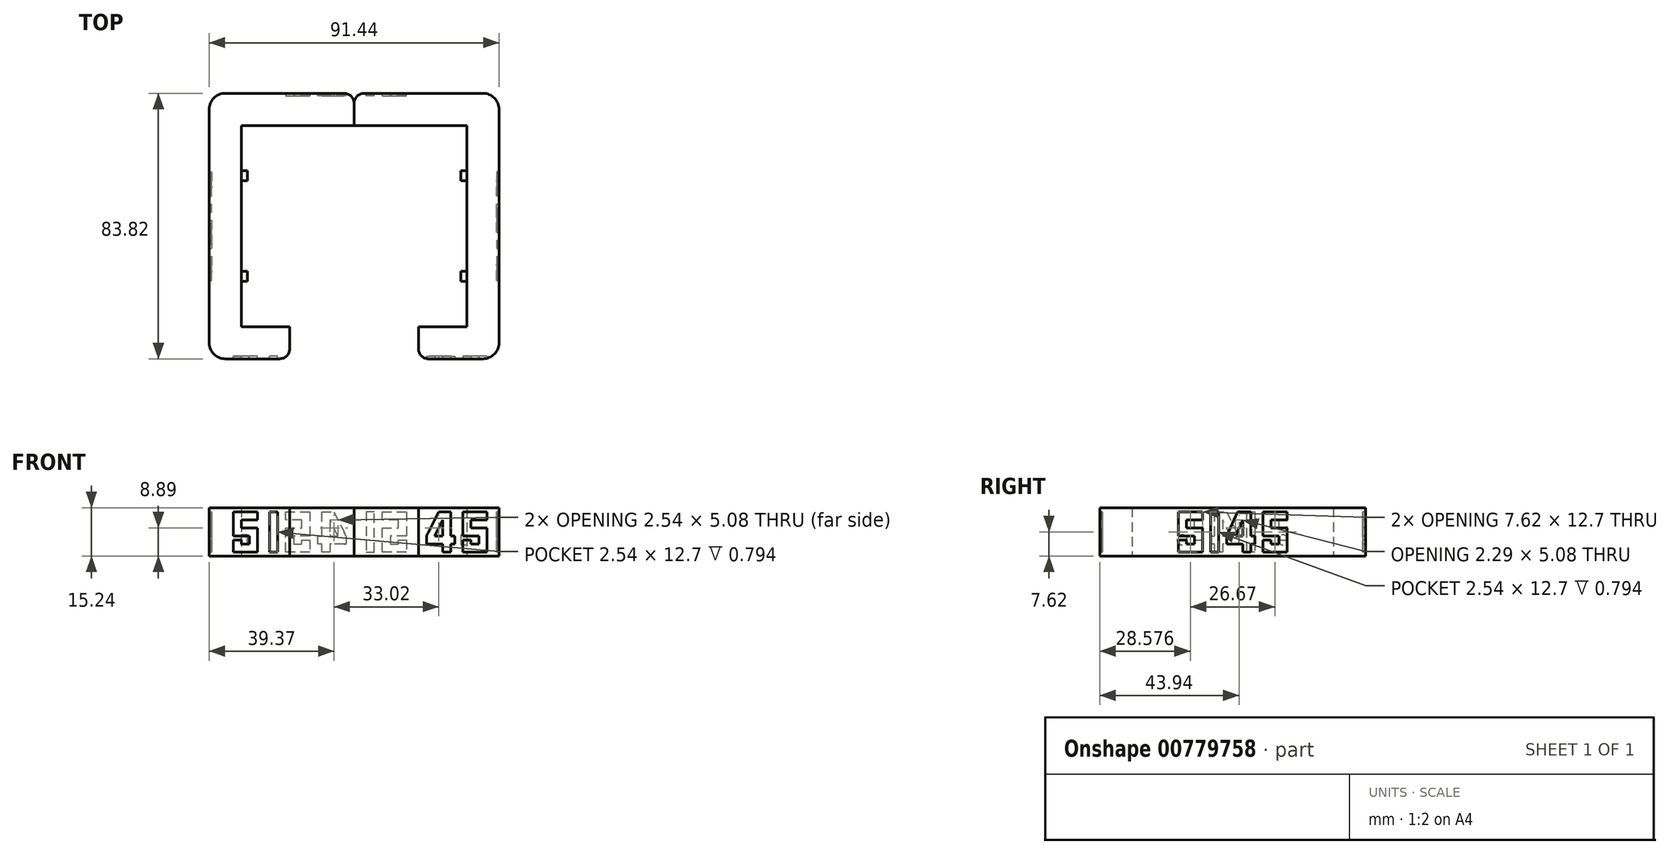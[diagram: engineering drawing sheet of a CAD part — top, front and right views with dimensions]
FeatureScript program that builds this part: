
annotation { "Feature Type Name" : "Feature", "Feature Type Description" : "" }
export const myFeature = defineFeature(function(context is Context, id is Id, definition is map)
    precondition{}
    {
        {
            var Q0;
            Q0=qCreatedBy(makeId("Top.planeOp"),FACE);
            var sketch = newSketch(context, id + "F0", { "sketchPlane" : qUnion([Q0])});
            skLineSegment(sketch, "E0", {"start": v(0, 28.67) * mm, "end": v(0, 38.83) * mm});
            skLineSegment(sketch, "E1", {"start": v(0, 38.83) * mm, "end": v(45.72, 38.83) * mm});
            skLineSegment(sketch, "E2", {"start": v(45.72, 38.83) * mm, "end": v(45.72, -44.99) * mm});
            skLineSegment(sketch, "E3", {"start": v(45.72, -44.99) * mm, "end": v(20.32, -44.99) * mm});
            skLineSegment(sketch, "E4", {"start": v(20.32, -44.99) * mm, "end": v(20.32, -34.83) * mm});
            skLineSegment(sketch, "E5", {"start": v(20.32, -34.83) * mm, "end": v(35.56, -34.83) * mm});
            skLineSegment(sketch, "E6", {"start": v(35.56, -34.83) * mm, "end": v(35.56, 28.67) * mm});
            skLineSegment(sketch, "E7", {"start": v(35.56, 28.67) * mm, "end": v(0, 28.67) * mm});
            skSolve(sketch);
        }
        {
            var Q0;
            Q0=makeQuery(id+"F0.imprint","IMPRINT",FACE,{"disambiguationData":[TD([[makeQuery(id+"F0.imprint","IMPRINT",EDGE,{"derivedFrom":sQuery(id+"F0.wireOp",EDGE,"E0")}),-1.0]])]});
            extrude(context, id + "F1", {"entities" : qUnion([Q0]), "depth" : 15.24 * mm, "offsetDistance" : 25.4 * mm});
        }
        {
            var Q0;
            Q0=makeQuery(id+"F1.opExtrude","SWEPT_FACE",FACE,{"disambiguationData":[OSD([sQuery(id+"F0.wireOp",EDGE,"E6")])]});
            var sketch = newSketch(context, id + "F2", { "sketchPlane" : qUnion([Q0])});
            skCircle(sketch, "E8", {"center": v(-12.8, 5.08) * mm, "radius": 1.59 * mm});
            skPoint(sketch, "E8.centerSnap0", {"position": v(-28.67, 5.08) * mm});
            skCircle(sketch, "E9", {"center": v(18.95, 5.08) * mm, "radius": 1.59 * mm});
            skPoint(sketch, "E9.centerSnap0", {"position": v(34.83, 5.08) * mm});
            skSolve(sketch);
        }
        {
            var Q0;
            Q0=makeQuery(id+"F2.imprint","IMPRINT",FACE,{"disambiguationData":[TD([[makeQuery(id+"F2.imprint","IMPRINT",EDGE,{"derivedFrom":sQuery(id+"F2.wireOp",EDGE,"E8")}),1.0]])]});
            var Q1;
            Q1=makeQuery(id+"F2.imprint","IMPRINT",FACE,{"disambiguationData":[TD([[makeQuery(id+"F2.imprint","IMPRINT",EDGE,{"derivedFrom":sQuery(id+"F2.wireOp",EDGE,"E9")}),1.0]])]});
            extrude(context, id + "F3", {"entities" : qUnion([Q0, Q1]), "operationType" : NewBodyOperationType.ADD, "depth" : 1.9 * mm, "offsetDistance" : 25.4 * mm});
        }
        {
            var Q0;
            Q0=qCreatedBy(makeId("Top.planeOp"),FACE);
            var sketch = newSketch(context, id + "F4", { "sketchPlane" : qUnion([Q0])});
            skLineSegment(sketch, "E10", {"start": v(0, 28.67) * mm, "end": v(-35.56, 28.67) * mm});
            skLineSegment(sketch, "E11", {"start": v(-35.56, 28.67) * mm, "end": v(-35.56, -34.83) * mm});
            skLineSegment(sketch, "E12", {"start": v(-35.56, -34.83) * mm, "end": v(-20.32, -34.83) * mm});
            skLineSegment(sketch, "E13", {"start": v(-20.32, -34.83) * mm, "end": v(-20.32, -44.99) * mm});
            skLineSegment(sketch, "E14", {"start": v(-20.32, -44.99) * mm, "end": v(-45.72, -44.99) * mm});
            skLineSegment(sketch, "E15", {"start": v(-45.72, -44.99) * mm, "end": v(-45.72, 38.83) * mm});
            skLineSegment(sketch, "E16", {"start": v(-45.72, 38.83) * mm, "end": v(0, 38.83) * mm});
            skLineSegment(sketch, "E17", {"start": v(0, 38.83) * mm, "end": v(0, 28.67) * mm});
            skSolve(sketch);
        }
        {
            var Q0;
            Q0=makeQuery(id+"F4.imprint","IMPRINT",FACE,{"disambiguationData":[TD([[makeQuery(id+"F4.imprint","IMPRINT",EDGE,{"derivedFrom":sQuery(id+"F4.wireOp",EDGE,"E10")}),-1.0]])]});
            extrude(context, id + "F5", {"entities" : qUnion([Q0]), "depth" : 15.24 * mm, "offsetDistance" : 25.4 * mm});
        }
        {
            var Q0;
            Q0=makeQuery(id+"F5.opExtrude","SWEPT_FACE",FACE,{"disambiguationData":[OSD([sQuery(id+"F4.wireOp",EDGE,"E11")])]});
            var sketch = newSketch(context, id + "F6", { "sketchPlane" : qUnion([Q0])});
            skCircle(sketch, "E18", {"center": v(-18.95, 5.08) * mm, "radius": 1.59 * mm});
            skPoint(sketch, "E18.centerSnap0", {"position": v(-34.83, 7.62) * mm});
            skCircle(sketch, "E19", {"center": v(12.8, 5.08) * mm, "radius": 1.59 * mm});
            skSolve(sketch);
        }
        {
            var Q0;
            Q0=makeQuery(id+"F6.imprint","IMPRINT",FACE,{"disambiguationData":[TD([[makeQuery(id+"F6.imprint","IMPRINT",EDGE,{"derivedFrom":sQuery(id+"F6.wireOp",EDGE,"E19")}),1.0]])]});
            var Q1;
            Q1=makeQuery(id+"F6.imprint","IMPRINT",FACE,{"disambiguationData":[TD([[makeQuery(id+"F6.imprint","IMPRINT",EDGE,{"derivedFrom":sQuery(id+"F6.wireOp",EDGE,"E18")}),1.0]])]});
            extrude(context, id + "F7", {"entities" : qUnion([Q0, Q1]), "operationType" : NewBodyOperationType.ADD, "depth" : 1.9 * mm, "offsetDistance" : 25.4 * mm});
        }
        {
            var Q0;
            Q0=makeQuery(id+"F1.opExtrude","SWEPT_FACE",FACE,{"disambiguationData":[OSD([sQuery(id+"F0.wireOp",EDGE,"E2")])]});
            var sketch = newSketch(context, id + "F8", { "sketchPlane" : qUnion([Q0])});
            skLineSegment(sketch, "E20", {"start": v(-12.6, 13.97) * mm, "end": v(-20.22, 13.97) * mm});
            skLineSegment(sketch, "E21", {"start": v(-20.22, 13.97) * mm, "end": v(-20.22, 6.35) * mm});
            skLineSegment(sketch, "E22", {"start": v(-20.22, 6.35) * mm, "end": v(-15.14, 6.35) * mm});
            skLineSegment(sketch, "E23", {"start": v(-15.14, 6.35) * mm, "end": v(-15.14, 3.81) * mm});
            skLineSegment(sketch, "E24", {"start": v(-15.14, 3.8) * mm, "end": v(-17.68, 3.8) * mm});
            skLineSegment(sketch, "E25", {"start": v(-17.68, 3.81) * mm, "end": v(-17.68, 5.08) * mm});
            skLineSegment(sketch, "E26", {"start": v(-17.68, 5.08) * mm, "end": v(-20.22, 5.08) * mm});
            skLineSegment(sketch, "E27", {"start": v(-20.22, 5.08) * mm, "end": v(-20.22, 1.27) * mm});
            skLineSegment(sketch, "E28", {"start": v(-20.22, 1.27) * mm, "end": v(-12.6, 1.27) * mm});
            skLineSegment(sketch, "E29", {"start": v(-12.6, 1.27) * mm, "end": v(-12.6, 8.9) * mm});
            skLineSegment(sketch, "E30", {"start": v(-12.6, 8.89) * mm, "end": v(-17.68, 8.89) * mm});
            skLineSegment(sketch, "E31", {"start": v(-17.68, 8.9) * mm, "end": v(-17.68, 11.43) * mm});
            skLineSegment(sketch, "E32", {"start": v(-17.68, 11.43) * mm, "end": v(-12.6, 11.43) * mm});
            skLineSegment(sketch, "E33", {"start": v(-12.6, 11.43) * mm, "end": v(-12.6, 13.97) * mm});
            skLineSegment(sketch, "E34", {"start": v(-10.06, 13.97) * mm, "end": v(-10.06, 1.27) * mm});
            skLineSegment(sketch, "E35", {"start": v(-10.06, 1.27) * mm, "end": v(-7.52, 1.27) * mm});
            skLineSegment(sketch, "E36", {"start": v(-7.52, 1.27) * mm, "end": v(-7.52, 13.97) * mm});
            skLineSegment(sketch, "E37", {"start": v(-7.52, 13.97) * mm, "end": v(-10.06, 13.97) * mm});
            skLineSegment(sketch, "E38", {"start": v(-1.54, 13.97) * mm, "end": v(-4.98, 6.35) * mm});
            skLineSegment(sketch, "E39", {"start": v(-4.98, 6.35) * mm, "end": v(-4.98, 3.81) * mm});
            skLineSegment(sketch, "E40", {"start": v(-4.98, 3.81) * mm, "end": v(0.1, 3.81) * mm});
            skLineSegment(sketch, "E41", {"start": v(0.1, 3.81) * mm, "end": v(0.1, 1.27) * mm});
            skLineSegment(sketch, "E42", {"start": v(0.1, 1.27) * mm, "end": v(2.64, 1.27) * mm});
            skLineSegment(sketch, "E43", {"start": v(2.64, 1.27) * mm, "end": v(2.64, 3.81) * mm});
            skLineSegment(sketch, "E44", {"start": v(2.64, 3.81) * mm, "end": v(3.9, 3.81) * mm});
            skLineSegment(sketch, "E45", {"start": v(3.9, 3.81) * mm, "end": v(3.9, 6.35) * mm});
            skLineSegment(sketch, "E46", {"start": v(3.9, 6.35) * mm, "end": v(2.64, 6.35) * mm});
            skLineSegment(sketch, "E47", {"start": v(2.64, 6.35) * mm, "end": v(2.64, 13.97) * mm});
            skLineSegment(sketch, "E48", {"start": v(2.64, 13.97) * mm, "end": v(-1.54, 13.97) * mm});
            skLineSegment(sketch, "E49", {"start": v(0.1, 6.35) * mm, "end": v(-2.2, 6.35) * mm});
            skLineSegment(sketch, "E50", {"start": v(-2.2, 6.35) * mm, "end": v(0.1, 11.43) * mm});
            skLineSegment(sketch, "E51", {"start": v(0.1, 11.43) * mm, "end": v(0.1, 6.35) * mm});
            skLineSegment(sketch, "E52", {"start": v(14.07, 13.97) * mm, "end": v(6.45, 13.97) * mm});
            skLineSegment(sketch, "E53", {"start": v(6.45, 13.97) * mm, "end": v(6.45, 6.35) * mm});
            skLineSegment(sketch, "E54", {"start": v(6.45, 6.35) * mm, "end": v(11.53, 6.35) * mm});
            skLineSegment(sketch, "E55", {"start": v(11.53, 6.35) * mm, "end": v(11.53, 3.81) * mm});
            skLineSegment(sketch, "E56", {"start": v(11.53, 3.81) * mm, "end": v(8.99, 3.81) * mm});
            skPoint(sketch, "E56.endSnap0", {"position": v(8.99, 6.35) * mm});
            skLineSegment(sketch, "E57", {"start": v(8.99, 3.81) * mm, "end": v(8.99, 5.08) * mm});
            skPoint(sketch, "E57.endSnap0", {"position": v(11.53, 5.08) * mm});
            skLineSegment(sketch, "E58", {"start": v(8.99, 5.08) * mm, "end": v(6.45, 5.08) * mm});
            skLineSegment(sketch, "E59", {"start": v(6.45, 5.08) * mm, "end": v(6.45, 1.27) * mm});
            skLineSegment(sketch, "E60", {"start": v(6.45, 1.27) * mm, "end": v(14.07, 1.27) * mm});
            skLineSegment(sketch, "E61", {"start": v(14.07, 1.27) * mm, "end": v(14.07, 8.9) * mm});
            skLineSegment(sketch, "E62", {"start": v(14.07, 8.9) * mm, "end": v(8.99, 8.9) * mm});
            skLineSegment(sketch, "E63", {"start": v(8.99, 8.9) * mm, "end": v(8.99, 11.43) * mm});
            skLineSegment(sketch, "E64", {"start": v(8.99, 11.43) * mm, "end": v(14.07, 11.43) * mm});
            skLineSegment(sketch, "E65", {"start": v(14.07, 11.43) * mm, "end": v(14.07, 13.97) * mm});
            skLineSegment(sketch, "E66", {"start": v(-20.22, 13.97) * mm, "end": v(-44.99, 13.97) * mm});
            skLineSegment(sketch, "E67", {"start": v(14.07, 13.97) * mm, "end": v(38.83, 13.97) * mm});
            skSolve(sketch);
        }
        {
            var Q0;
            Q0=makeQuery(id+"F8.imprint","IMPRINT",FACE,{"disambiguationData":[TD([[makeQuery(id+"F8.imprint","IMPRINT",EDGE,{"derivedFrom":sQuery(id+"F8.wireOp",EDGE,"E20")}),1.0]])]});
            var Q1;
            Q1=makeQuery(id+"F8.imprint","IMPRINT",FACE,{"disambiguationData":[TD([[makeQuery(id+"F8.imprint","IMPRINT",EDGE,{"derivedFrom":sQuery(id+"F8.wireOp",EDGE,"E34")}),1.0]])]});
            var Q2;
            Q2=makeQuery(id+"F8.imprint","IMPRINT",FACE,{"disambiguationData":[TD([[makeQuery(id+"F8.imprint","IMPRINT",EDGE,{"derivedFrom":sQuery(id+"F8.wireOp",EDGE,"E38")}),1.0]])]});
            var Q3;
            Q3=makeQuery(id+"F8.imprint","IMPRINT",FACE,{"disambiguationData":[TD([[makeQuery(id+"F8.imprint","IMPRINT",EDGE,{"derivedFrom":sQuery(id+"F8.wireOp",EDGE,"E52")}),1.0]])]});
            extrude(context, id + "F9", {"entities" : qUnion([Q0, Q1, Q2, Q3]), "operationType" : NewBodyOperationType.REMOVE, "oppositeDirection" : true, "depth" : 0.8 * mm, "offsetDistance" : 25.4 * mm});
        }
        {
            var Q0;
            Q0=makeQuery(id+"F1.opExtrude","SWEPT_FACE",FACE,{"disambiguationData":[OSD([sQuery(id+"F0.wireOp",EDGE,"E3")])]});
            var sketch = newSketch(context, id + "F10", { "sketchPlane" : qUnion([Q0])});
            skLineSegment(sketch, "E68", {"start": v(22.86, 6.35) * mm, "end": v(22.86, 3.81) * mm});
            skLineSegment(sketch, "E69", {"start": v(22.86, 3.81) * mm, "end": v(27.94, 3.81) * mm});
            skLineSegment(sketch, "E70", {"start": v(27.94, 3.81) * mm, "end": v(27.94, 1.27) * mm});
            skLineSegment(sketch, "E71", {"start": v(27.94, 1.27) * mm, "end": v(30.48, 1.27) * mm});
            skLineSegment(sketch, "E72", {"start": v(30.48, 1.27) * mm, "end": v(30.48, 3.81) * mm});
            skLineSegment(sketch, "E73", {"start": v(30.48, 3.81) * mm, "end": v(31.75, 3.81) * mm});
            skLineSegment(sketch, "E74", {"start": v(31.75, 3.81) * mm, "end": v(31.75, 6.35) * mm});
            skLineSegment(sketch, "E75", {"start": v(31.75, 6.35) * mm, "end": v(30.48, 6.35) * mm});
            skLineSegment(sketch, "E76", {"start": v(30.48, 6.35) * mm, "end": v(30.48, 13.97) * mm});
            skLineSegment(sketch, "E77", {"start": v(30.48, 13.97) * mm, "end": v(26.67, 13.97) * mm});
            skLineSegment(sketch, "E78", {"start": v(26.67, 13.97) * mm, "end": v(22.86, 6.35) * mm});
            skLineSegment(sketch, "E79", {"start": v(27.94, 6.35) * mm, "end": v(25.4, 6.35) * mm});
            skLineSegment(sketch, "E80", {"start": v(25.4, 6.35) * mm, "end": v(27.94, 11.43) * mm});
            skLineSegment(sketch, "E81", {"start": v(27.94, 11.43) * mm, "end": v(27.94, 6.35) * mm});
            skLineSegment(sketch, "E82", {"start": v(41.91, 13.97) * mm, "end": v(34.3, 13.97) * mm});
            skLineSegment(sketch, "E83", {"start": v(34.3, 13.97) * mm, "end": v(34.3, 6.35) * mm});
            skLineSegment(sketch, "E84", {"start": v(34.3, 6.35) * mm, "end": v(39.37, 6.35) * mm});
            skLineSegment(sketch, "E85", {"start": v(39.37, 6.35) * mm, "end": v(39.37, 3.81) * mm});
            skLineSegment(sketch, "E86", {"start": v(39.37, 3.81) * mm, "end": v(36.83, 3.81) * mm});
            skPoint(sketch, "E86.endSnap0", {"position": v(36.83, 6.35) * mm});
            skLineSegment(sketch, "E87", {"start": v(36.83, 3.81) * mm, "end": v(36.83, 5.08) * mm});
            skPoint(sketch, "E87.endSnap0", {"position": v(39.37, 5.08) * mm});
            skLineSegment(sketch, "E88", {"start": v(36.83, 5.08) * mm, "end": v(34.3, 5.08) * mm});
            skLineSegment(sketch, "E89", {"start": v(34.3, 5.08) * mm, "end": v(34.3, 1.27) * mm});
            skLineSegment(sketch, "E90", {"start": v(34.3, 1.27) * mm, "end": v(41.91, 1.27) * mm});
            skLineSegment(sketch, "E91", {"start": v(41.91, 1.27) * mm, "end": v(41.91, 8.89) * mm});
            skLineSegment(sketch, "E92", {"start": v(41.91, 8.89) * mm, "end": v(36.83, 8.89) * mm});
            skLineSegment(sketch, "E93", {"start": v(36.83, 8.89) * mm, "end": v(36.83, 11.43) * mm});
            skLineSegment(sketch, "E94", {"start": v(36.83, 11.43) * mm, "end": v(41.91, 11.43) * mm});
            skLineSegment(sketch, "E95", {"start": v(41.91, 11.43) * mm, "end": v(41.91, 13.97) * mm});
            skSolve(sketch);
        }
        {
            var Q0;
            Q0=makeQuery(id+"F10.imprint","IMPRINT",FACE,{"disambiguationData":[TD([[makeQuery(id+"F10.imprint","IMPRINT",EDGE,{"derivedFrom":sQuery(id+"F10.wireOp",EDGE,"E68")}),1.0]])]});
            var Q1;
            Q1=makeQuery(id+"F10.imprint","IMPRINT",FACE,{"disambiguationData":[TD([[makeQuery(id+"F10.imprint","IMPRINT",EDGE,{"derivedFrom":sQuery(id+"F10.wireOp",EDGE,"E82")}),1.0]])]});
            extrude(context, id + "F11", {"entities" : qUnion([Q0, Q1]), "operationType" : NewBodyOperationType.REMOVE, "oppositeDirection" : true, "depth" : 0.8 * mm, "offsetDistance" : 25.4 * mm});
        }
        {
            var Q0;
            Q0=makeQuery(id+"F5.opExtrude","SWEPT_FACE",FACE,{"disambiguationData":[OSD([sQuery(id+"F4.wireOp",EDGE,"E14")])]});
            var sketch = newSketch(context, id + "F12", { "sketchPlane" : qUnion([Q0])});
            skLineSegment(sketch, "E96", {"start": v(-24.13, 13.97) * mm, "end": v(-26.67, 13.97) * mm});
            skLineSegment(sketch, "E97", {"start": v(-26.67, 13.97) * mm, "end": v(-26.67, 1.27) * mm});
            skLineSegment(sketch, "E98", {"start": v(-26.67, 1.27) * mm, "end": v(-24.13, 1.27) * mm});
            skLineSegment(sketch, "E99", {"start": v(-24.13, 1.27) * mm, "end": v(-24.13, 13.97) * mm});
            skLineSegment(sketch, "E100", {"start": v(-30.48, 13.97) * mm, "end": v(-38.1, 13.97) * mm});
            skLineSegment(sketch, "E101", {"start": v(-38.1, 13.97) * mm, "end": v(-38.1, 6.35) * mm});
            skLineSegment(sketch, "E102", {"start": v(-38.1, 6.35) * mm, "end": v(-33.02, 6.35) * mm});
            skLineSegment(sketch, "E103", {"start": v(-33.02, 6.35) * mm, "end": v(-33.02, 3.8) * mm});
            skLineSegment(sketch, "E104", {"start": v(-33.02, 3.8) * mm, "end": v(-35.56, 3.8) * mm});
            skLineSegment(sketch, "E105", {"start": v(-35.56, 3.8) * mm, "end": v(-35.56, 5.08) * mm});
            skLineSegment(sketch, "E106", {"start": v(-35.56, 5.08) * mm, "end": v(-38.1, 5.08) * mm});
            skLineSegment(sketch, "E107", {"start": v(-38.1, 5.08) * mm, "end": v(-38.1, 1.27) * mm});
            skLineSegment(sketch, "E108", {"start": v(-38.1, 1.27) * mm, "end": v(-30.48, 1.27) * mm});
            skLineSegment(sketch, "E109", {"start": v(-30.48, 1.27) * mm, "end": v(-30.48, 8.9) * mm});
            skLineSegment(sketch, "E110", {"start": v(-30.48, 8.89) * mm, "end": v(-35.56, 8.89) * mm});
            skLineSegment(sketch, "E111", {"start": v(-35.56, 8.89) * mm, "end": v(-35.56, 11.43) * mm});
            skLineSegment(sketch, "E112", {"start": v(-35.56, 11.43) * mm, "end": v(-30.48, 11.43) * mm});
            skLineSegment(sketch, "E113", {"start": v(-30.48, 11.43) * mm, "end": v(-30.48, 13.97) * mm});
            skSolve(sketch);
        }
        {
            var Q0;
            Q0=makeQuery(id+"F12.imprint","IMPRINT",FACE,{"disambiguationData":[TD([[makeQuery(id+"F12.imprint","IMPRINT",EDGE,{"derivedFrom":sQuery(id+"F12.wireOp",EDGE,"E100")}),1.0]])]});
            var Q1;
            Q1=makeQuery(id+"F12.imprint","IMPRINT",FACE,{"disambiguationData":[TD([[makeQuery(id+"F12.imprint","IMPRINT",EDGE,{"derivedFrom":sQuery(id+"F12.wireOp",EDGE,"E96")}),1.0]])]});
            extrude(context, id + "F13", {"entities" : qUnion([Q0, Q1]), "operationType" : NewBodyOperationType.REMOVE, "oppositeDirection" : true, "depth" : 0.8 * mm, "offsetDistance" : 25.4 * mm});
        }
        {
            var Q0;
            Q0=makeQuery(id+"F5.opExtrude","SWEPT_FACE",FACE,{"disambiguationData":[OSD([sQuery(id+"F4.wireOp",EDGE,"E15")])]});
            var sketch = newSketch(context, id + "F14", { "sketchPlane" : qUnion([Q0])});
            skLineSegment(sketch, "E114", {"start": v(-6.45, 13.97) * mm, "end": v(-14.07, 13.97) * mm});
            skLineSegment(sketch, "E115", {"start": v(-14.07, 13.97) * mm, "end": v(-14.07, 6.35) * mm});
            skLineSegment(sketch, "E116", {"start": v(-14.07, 6.35) * mm, "end": v(-8.99, 6.35) * mm});
            skLineSegment(sketch, "E117", {"start": v(-8.99, 6.35) * mm, "end": v(-8.99, 3.8) * mm});
            skLineSegment(sketch, "E118", {"start": v(-8.99, 3.81) * mm, "end": v(-11.53, 3.81) * mm});
            skLineSegment(sketch, "E119", {"start": v(-11.53, 3.8) * mm, "end": v(-11.53, 5.08) * mm});
            skLineSegment(sketch, "E120", {"start": v(-11.53, 5.08) * mm, "end": v(-14.07, 5.08) * mm});
            skLineSegment(sketch, "E121", {"start": v(-14.07, 5.08) * mm, "end": v(-14.07, 1.27) * mm});
            skLineSegment(sketch, "E122", {"start": v(-14.07, 1.27) * mm, "end": v(-6.45, 1.27) * mm});
            skLineSegment(sketch, "E123", {"start": v(-6.45, 1.27) * mm, "end": v(-6.45, 8.9) * mm});
            skLineSegment(sketch, "E124", {"start": v(-6.45, 8.9) * mm, "end": v(-11.53, 8.9) * mm});
            skLineSegment(sketch, "E125", {"start": v(-11.53, 8.89) * mm, "end": v(-11.53, 11.43) * mm});
            skLineSegment(sketch, "E126", {"start": v(-11.53, 11.43) * mm, "end": v(-6.45, 11.43) * mm});
            skLineSegment(sketch, "E127", {"start": v(-6.45, 11.43) * mm, "end": v(-6.45, 13.97) * mm});
            skLineSegment(sketch, "E128", {"start": v(-3.9, 13.97) * mm, "end": v(-3.9, 1.27) * mm});
            skLineSegment(sketch, "E129", {"start": v(-3.9, 1.27) * mm, "end": v(-1.37, 1.27) * mm});
            skLineSegment(sketch, "E130", {"start": v(-1.37, 1.27) * mm, "end": v(-1.37, 13.97) * mm});
            skLineSegment(sketch, "E131", {"start": v(-1.37, 13.97) * mm, "end": v(-3.9, 13.97) * mm});
            skLineSegment(sketch, "E132", {"start": v(4.98, 13.97) * mm, "end": v(1.17, 6.35) * mm});
            skLineSegment(sketch, "E133", {"start": v(1.17, 6.35) * mm, "end": v(1.17, 3.81) * mm});
            skLineSegment(sketch, "E134", {"start": v(1.17, 3.81) * mm, "end": v(6.25, 3.81) * mm});
            skLineSegment(sketch, "E135", {"start": v(6.25, 3.81) * mm, "end": v(6.25, 1.27) * mm});
            skLineSegment(sketch, "E136", {"start": v(6.25, 1.27) * mm, "end": v(8.8, 1.27) * mm});
            skLineSegment(sketch, "E137", {"start": v(8.8, 1.27) * mm, "end": v(8.8, 3.81) * mm});
            skLineSegment(sketch, "E138", {"start": v(8.8, 3.81) * mm, "end": v(10.06, 3.81) * mm});
            skLineSegment(sketch, "E139", {"start": v(10.06, 3.81) * mm, "end": v(10.06, 6.35) * mm});
            skLineSegment(sketch, "E140", {"start": v(10.06, 6.35) * mm, "end": v(8.8, 6.35) * mm});
            skLineSegment(sketch, "E141", {"start": v(8.8, 6.35) * mm, "end": v(8.8, 13.97) * mm});
            skLineSegment(sketch, "E142", {"start": v(8.8, 13.97) * mm, "end": v(4.98, 13.97) * mm});
            skLineSegment(sketch, "E143", {"start": v(6.25, 6.35) * mm, "end": v(3.71, 6.35) * mm});
            skLineSegment(sketch, "E144", {"start": v(3.71, 6.35) * mm, "end": v(6.25, 11.43) * mm});
            skLineSegment(sketch, "E145", {"start": v(6.25, 11.43) * mm, "end": v(6.25, 6.35) * mm});
            skLineSegment(sketch, "E146", {"start": v(20.22, 13.97) * mm, "end": v(12.6, 13.97) * mm});
            skLineSegment(sketch, "E147", {"start": v(12.6, 13.97) * mm, "end": v(12.6, 6.35) * mm});
            skLineSegment(sketch, "E148", {"start": v(12.6, 6.35) * mm, "end": v(17.68, 6.35) * mm});
            skLineSegment(sketch, "E149", {"start": v(17.68, 6.35) * mm, "end": v(17.68, 3.81) * mm});
            skLineSegment(sketch, "E150", {"start": v(17.68, 3.81) * mm, "end": v(15.14, 3.81) * mm});
            skLineSegment(sketch, "E151", {"start": v(15.14, 3.81) * mm, "end": v(15.14, 5.08) * mm});
            skLineSegment(sketch, "E152", {"start": v(15.14, 5.08) * mm, "end": v(12.6, 5.08) * mm});
            skLineSegment(sketch, "E153", {"start": v(12.6, 5.08) * mm, "end": v(12.6, 1.27) * mm});
            skLineSegment(sketch, "E154", {"start": v(12.6, 1.27) * mm, "end": v(20.22, 1.27) * mm});
            skLineSegment(sketch, "E155", {"start": v(20.22, 1.27) * mm, "end": v(20.22, 8.9) * mm});
            skLineSegment(sketch, "E156", {"start": v(20.22, 8.9) * mm, "end": v(15.14, 8.9) * mm});
            skLineSegment(sketch, "E157", {"start": v(15.14, 8.9) * mm, "end": v(15.14, 11.43) * mm});
            skLineSegment(sketch, "E158", {"start": v(15.14, 11.43) * mm, "end": v(20.22, 11.43) * mm});
            skLineSegment(sketch, "E159", {"start": v(20.22, 11.43) * mm, "end": v(20.22, 13.97) * mm});
            skLineSegment(sketch, "E160", {"start": v(-38.83, 13.97) * mm, "end": v(-14.07, 13.97) * mm});
            skLineSegment(sketch, "E161", {"start": v(44.99, 13.97) * mm, "end": v(20.22, 13.97) * mm});
            skSolve(sketch);
        }
        {
            var Q0;
            Q0=qSketchRegion(id+"F14",true);
            extrude(context, id + "F15", {"entities" : qUnion([Q0]), "operationType" : NewBodyOperationType.REMOVE, "oppositeDirection" : true, "depth" : 0.8 * mm, "offsetDistance" : 25.4 * mm});
        }
        {
            var Q0;
            Q0=makeQuery(id+"F1.opExtrude","SWEPT_FACE",FACE,{"disambiguationData":[OSD([sQuery(id+"F0.wireOp",EDGE,"E1")])]});
            var sketch = newSketch(context, id + "F16", { "sketchPlane" : qUnion([Q0])});
            skLineSegment(sketch, "E162", {"start": v(-8.9, 13.97) * mm, "end": v(-16.51, 13.97) * mm});
            skLineSegment(sketch, "E163", {"start": v(-16.51, 13.97) * mm, "end": v(-16.51, 6.35) * mm});
            skLineSegment(sketch, "E164", {"start": v(-16.51, 6.35) * mm, "end": v(-11.43, 6.35) * mm});
            skLineSegment(sketch, "E165", {"start": v(-11.43, 6.35) * mm, "end": v(-11.43, 3.81) * mm});
            skLineSegment(sketch, "E166", {"start": v(-11.43, 3.81) * mm, "end": v(-13.97, 3.8) * mm});
            skLineSegment(sketch, "E167", {"start": v(-13.97, 3.8) * mm, "end": v(-13.97, 5.08) * mm});
            skLineSegment(sketch, "E168", {"start": v(-13.97, 5.08) * mm, "end": v(-16.51, 5.08) * mm});
            skLineSegment(sketch, "E169", {"start": v(-16.51, 5.08) * mm, "end": v(-16.51, 1.27) * mm});
            skLineSegment(sketch, "E170", {"start": v(-16.51, 1.27) * mm, "end": v(-8.9, 1.27) * mm});
            skLineSegment(sketch, "E171", {"start": v(-8.9, 1.27) * mm, "end": v(-8.9, 8.89) * mm});
            skLineSegment(sketch, "E172", {"start": v(-8.9, 8.9) * mm, "end": v(-13.97, 8.89) * mm});
            skLineSegment(sketch, "E173", {"start": v(-13.97, 8.89) * mm, "end": v(-13.97, 11.43) * mm});
            skLineSegment(sketch, "E174", {"start": v(-13.97, 11.43) * mm, "end": v(-8.9, 11.43) * mm});
            skLineSegment(sketch, "E175", {"start": v(-8.9, 11.43) * mm, "end": v(-8.9, 13.97) * mm});
            skLineSegment(sketch, "E176", {"start": v(-6.35, 13.97) * mm, "end": v(-3.81, 13.97) * mm});
            skLineSegment(sketch, "E177", {"start": v(-3.81, 13.97) * mm, "end": v(-3.81, 1.27) * mm});
            skLineSegment(sketch, "E178", {"start": v(-3.81, 1.27) * mm, "end": v(-6.35, 1.27) * mm});
            skLineSegment(sketch, "E179", {"start": v(-6.35, 1.27) * mm, "end": v(-6.35, 13.97) * mm});
            skSolve(sketch);
        }
        {
            var Q0;
            Q0=qSketchRegion(id+"F16",true);
            extrude(context, id + "F17", {"entities" : qUnion([Q0]), "operationType" : NewBodyOperationType.REMOVE, "oppositeDirection" : true, "depth" : 0.8 * mm, "offsetDistance" : 25.4 * mm});
        }
        {
            var Q0;
            Q0=makeQuery(id+"F5.opExtrude","SWEPT_FACE",FACE,{"disambiguationData":[OSD([sQuery(id+"F4.wireOp",EDGE,"E16")])]});
            var sketch = newSketch(context, id + "F18", { "sketchPlane" : qUnion([Q0])});
            skLineSegment(sketch, "E180", {"start": v(2.54, 6.35) * mm, "end": v(2.54, 3.81) * mm});
            skLineSegment(sketch, "E181", {"start": v(2.54, 3.81) * mm, "end": v(7.62, 3.81) * mm});
            skLineSegment(sketch, "E182", {"start": v(7.62, 3.81) * mm, "end": v(7.62, 1.27) * mm});
            skLineSegment(sketch, "E183", {"start": v(7.62, 1.27) * mm, "end": v(10.16, 1.27) * mm});
            skLineSegment(sketch, "E184", {"start": v(10.16, 1.27) * mm, "end": v(10.16, 3.81) * mm});
            skLineSegment(sketch, "E185", {"start": v(10.16, 3.81) * mm, "end": v(11.43, 3.81) * mm});
            skLineSegment(sketch, "E186", {"start": v(11.43, 3.81) * mm, "end": v(11.43, 6.35) * mm});
            skLineSegment(sketch, "E187", {"start": v(11.43, 6.35) * mm, "end": v(10.16, 6.35) * mm});
            skLineSegment(sketch, "E188", {"start": v(10.16, 6.35) * mm, "end": v(10.16, 13.97) * mm});
            skLineSegment(sketch, "E189", {"start": v(10.16, 13.97) * mm, "end": v(6.35, 13.97) * mm});
            skLineSegment(sketch, "E190", {"start": v(6.35, 13.97) * mm, "end": v(2.54, 6.35) * mm});
            skLineSegment(sketch, "E191", {"start": v(7.62, 6.35) * mm, "end": v(5.08, 6.35) * mm});
            skLineSegment(sketch, "E192", {"start": v(5.08, 6.35) * mm, "end": v(7.62, 11.43) * mm});
            skLineSegment(sketch, "E193", {"start": v(7.62, 11.43) * mm, "end": v(7.62, 6.35) * mm});
            skLineSegment(sketch, "E194", {"start": v(21.6, 13.97) * mm, "end": v(13.97, 13.97) * mm});
            skLineSegment(sketch, "E195", {"start": v(13.97, 13.97) * mm, "end": v(13.97, 6.35) * mm});
            skLineSegment(sketch, "E196", {"start": v(13.97, 6.35) * mm, "end": v(19.05, 6.35) * mm});
            skLineSegment(sketch, "E197", {"start": v(19.05, 6.35) * mm, "end": v(19.05, 3.81) * mm});
            skLineSegment(sketch, "E198", {"start": v(19.05, 3.81) * mm, "end": v(16.51, 3.81) * mm});
            skLineSegment(sketch, "E199", {"start": v(16.51, 3.81) * mm, "end": v(16.51, 5.08) * mm});
            skLineSegment(sketch, "E200", {"start": v(16.51, 5.08) * mm, "end": v(13.97, 5.08) * mm});
            skLineSegment(sketch, "E201", {"start": v(13.97, 5.08) * mm, "end": v(13.97, 1.27) * mm});
            skLineSegment(sketch, "E202", {"start": v(13.97, 1.27) * mm, "end": v(21.59, 1.27) * mm});
            skLineSegment(sketch, "E203", {"start": v(21.59, 1.27) * mm, "end": v(21.59, 8.9) * mm});
            skLineSegment(sketch, "E204", {"start": v(21.59, 8.9) * mm, "end": v(16.51, 8.9) * mm});
            skLineSegment(sketch, "E205", {"start": v(16.51, 8.9) * mm, "end": v(16.51, 11.43) * mm});
            skLineSegment(sketch, "E206", {"start": v(16.51, 11.43) * mm, "end": v(21.59, 11.43) * mm});
            skLineSegment(sketch, "E207", {"start": v(21.59, 11.43) * mm, "end": v(21.59, 13.97) * mm});
            skSolve(sketch);
        }
        {
            var Q0;
            Q0=qSketchRegion(id+"F18",true);
            extrude(context, id + "F19", {"entities" : qUnion([Q0]), "operationType" : NewBodyOperationType.REMOVE, "oppositeDirection" : true, "depth" : 0.8 * mm, "offsetDistance" : 25.4 * mm});
        }
        {
            var Q0;
            Q0=makeQuery(id+"F5.opExtrude","SWEPT_EDGE",EDGE,{"disambiguationData":[OSD([sQuery(id+"F4.wireOp",EDGE,"E15"),sQuery(id+"F4.wireOp",EDGE,"E16")])]});
            var Q1;
            Q1=makeQuery(id+"F5.opExtrude","SWEPT_EDGE",EDGE,{"disambiguationData":[OSD([sQuery(id+"F4.wireOp",EDGE,"E14"),sQuery(id+"F4.wireOp",EDGE,"E15")])]});
            fillet(context, id + "F20", {"entities" : qUnion([Q0, Q1]), "tangentPropagation" : true, "radius" : 5.08 * mm, "defaultsChanged" : true, "vertexSettings" : [], "allowEdgeOverflow" : false});
        }
        {
            var Q0;
            Q0=makeQuery(id+"F1.opExtrude","SWEPT_EDGE",EDGE,{"disambiguationData":[OSD([sQuery(id+"F0.wireOp",EDGE,"E2"),sQuery(id+"F0.wireOp",EDGE,"E3")])]});
            var Q1;
            Q1=makeQuery(id+"F1.opExtrude","SWEPT_EDGE",EDGE,{"disambiguationData":[OSD([sQuery(id+"F0.wireOp",EDGE,"E1"),sQuery(id+"F0.wireOp",EDGE,"E2")])]});
            fillet(context, id + "F21", {"entities" : qUnion([Q0, Q1]), "tangentPropagation" : true, "radius" : 5.08 * mm, "defaultsChanged" : false, "vertexSettings" : [], "allowEdgeOverflow" : false});
        }
        {
            var Q0;
            Q0=makeQuery(id+"F1.opExtrude","SWEPT_EDGE",EDGE,{"disambiguationData":[OSD([sQuery(id+"F0.wireOp",EDGE,"E3"),sQuery(id+"F0.wireOp",EDGE,"E4")])]});
            var Q1;
            Q1=makeQuery(id+"F5.opExtrude","SWEPT_EDGE",EDGE,{"disambiguationData":[OSD([sQuery(id+"F4.wireOp",EDGE,"E13"),sQuery(id+"F4.wireOp",EDGE,"E14")])]});
            var Q2;
            Q2=makeQuery(id+"F1.opExtrude","SWEPT_EDGE",EDGE,{"disambiguationData":[OSD([sQuery(id+"F0.wireOp",EDGE,"E0"),sQuery(id+"F0.wireOp",EDGE,"E1")])]});
            var Q3;
            Q3=makeQuery(id+"F5.opExtrude","SWEPT_EDGE",EDGE,{"disambiguationData":[OSD([sQuery(id+"F4.wireOp",EDGE,"E16"),sQuery(id+"F4.wireOp",EDGE,"E17")])]});
            fillet(context, id + "F22", {"entities" : qUnion([Q0, Q1, Q2, Q3]), "tangentPropagation" : true, "radius" : 3.17 * mm, "defaultsChanged" : true, "vertexSettings" : [], "allowEdgeOverflow" : false});
        }
        {
            var Q0;
            Q0=makeQuery(id+"F11.boolean.opBoolean","COPY",FACE,{"derivedFrom":makeQuery(id+"F11.opExtrude","CAP_FACE",FACE,{"disambiguationData":[OSD([sQuery(id+"F10.wireOp",EDGE,"E68"),sQuery(id+"F10.wireOp",EDGE,"E69"),sQuery(id+"F10.wireOp",EDGE,"E70"),sQuery(id+"F10.wireOp",EDGE,"E71"),sQuery(id+"F10.wireOp",EDGE,"E72"),sQuery(id+"F10.wireOp",EDGE,"E73"),sQuery(id+"F10.wireOp",EDGE,"E74"),sQuery(id+"F10.wireOp",EDGE,"E75"),sQuery(id+"F10.wireOp",EDGE,"E76"),sQuery(id+"F10.wireOp",EDGE,"E77"),sQuery(id+"F10.wireOp",EDGE,"E78"),sQuery(id+"F10.wireOp",EDGE,"E79"),sQuery(id+"F10.wireOp",EDGE,"E80"),sQuery(id+"F10.wireOp",EDGE,"E81")])],"isStart":false})});
            var Q1;
            Q1=makeQuery(id+"F11.boolean.opBoolean","COPY",FACE,{"derivedFrom":makeQuery(id+"F11.opExtrude","CAP_FACE",FACE,{"disambiguationData":[OSD([sQuery(id+"F10.wireOp",EDGE,"E82"),sQuery(id+"F10.wireOp",EDGE,"E83"),sQuery(id+"F10.wireOp",EDGE,"E84"),sQuery(id+"F10.wireOp",EDGE,"E85"),sQuery(id+"F10.wireOp",EDGE,"E86"),sQuery(id+"F10.wireOp",EDGE,"E87"),sQuery(id+"F10.wireOp",EDGE,"E88"),sQuery(id+"F10.wireOp",EDGE,"E89"),sQuery(id+"F10.wireOp",EDGE,"E90"),sQuery(id+"F10.wireOp",EDGE,"E91"),sQuery(id+"F10.wireOp",EDGE,"E92"),sQuery(id+"F10.wireOp",EDGE,"E93"),sQuery(id+"F10.wireOp",EDGE,"E94"),sQuery(id+"F10.wireOp",EDGE,"E95")])],"isStart":false})});
            var Q2;
            Q2=makeQuery(id+"F13.boolean.opBoolean","COPY",FACE,{"derivedFrom":makeQuery(id+"F13.opExtrude","CAP_FACE",FACE,{"disambiguationData":[OSD([sQuery(id+"F12.wireOp",EDGE,"E96"),sQuery(id+"F12.wireOp",EDGE,"E97"),sQuery(id+"F12.wireOp",EDGE,"E98"),sQuery(id+"F12.wireOp",EDGE,"E99")])],"isStart":false})});
            var Q3;
            Q3=makeQuery(id+"F13.boolean.opBoolean","COPY",FACE,{"derivedFrom":makeQuery(id+"F13.opExtrude","CAP_FACE",FACE,{"disambiguationData":[OSD([sQuery(id+"F12.wireOp",EDGE,"E100"),sQuery(id+"F12.wireOp",EDGE,"E101"),sQuery(id+"F12.wireOp",EDGE,"E102"),sQuery(id+"F12.wireOp",EDGE,"E103"),sQuery(id+"F12.wireOp",EDGE,"E104"),sQuery(id+"F12.wireOp",EDGE,"E105"),sQuery(id+"F12.wireOp",EDGE,"E106"),sQuery(id+"F12.wireOp",EDGE,"E107"),sQuery(id+"F12.wireOp",EDGE,"E108"),sQuery(id+"F12.wireOp",EDGE,"E109"),sQuery(id+"F12.wireOp",EDGE,"E110"),sQuery(id+"F12.wireOp",EDGE,"E111"),sQuery(id+"F12.wireOp",EDGE,"E112"),sQuery(id+"F12.wireOp",EDGE,"E113")])],"isStart":false})});
            extrude(context, id + "F23", {"entities" : qUnion([Q0, Q1, Q2, Q3]), "depth" : 0.8 * mm, "offsetDistance" : 25.4 * mm});
        }
        {
            var Q0;
            Q0=makeQuery(id+"F15.boolean.opBoolean","COPY",FACE,{"derivedFrom":makeQuery(id+"F15.opExtrude","CAP_FACE",FACE,{"disambiguationData":[OSD([sQuery(id+"F14.wireOp",EDGE,"E114"),sQuery(id+"F14.wireOp",EDGE,"E115"),sQuery(id+"F14.wireOp",EDGE,"E116"),sQuery(id+"F14.wireOp",EDGE,"E117"),sQuery(id+"F14.wireOp",EDGE,"E118"),sQuery(id+"F14.wireOp",EDGE,"E119"),sQuery(id+"F14.wireOp",EDGE,"E120"),sQuery(id+"F14.wireOp",EDGE,"E121"),sQuery(id+"F14.wireOp",EDGE,"E122"),sQuery(id+"F14.wireOp",EDGE,"E123"),sQuery(id+"F14.wireOp",EDGE,"E124"),sQuery(id+"F14.wireOp",EDGE,"E125"),sQuery(id+"F14.wireOp",EDGE,"E126"),sQuery(id+"F14.wireOp",EDGE,"E127")])],"isStart":false})});
            var Q1;
            Q1=makeQuery(id+"F15.boolean.opBoolean","COPY",FACE,{"derivedFrom":makeQuery(id+"F15.opExtrude","CAP_FACE",FACE,{"disambiguationData":[OSD([sQuery(id+"F14.wireOp",EDGE,"E128"),sQuery(id+"F14.wireOp",EDGE,"E129"),sQuery(id+"F14.wireOp",EDGE,"E130"),sQuery(id+"F14.wireOp",EDGE,"E131")])],"isStart":false})});
            var Q2;
            Q2=makeQuery(id+"F15.boolean.opBoolean","COPY",FACE,{"derivedFrom":makeQuery(id+"F15.opExtrude","CAP_FACE",FACE,{"disambiguationData":[OSD([sQuery(id+"F14.wireOp",EDGE,"E132"),sQuery(id+"F14.wireOp",EDGE,"E133"),sQuery(id+"F14.wireOp",EDGE,"E134"),sQuery(id+"F14.wireOp",EDGE,"E135"),sQuery(id+"F14.wireOp",EDGE,"E136"),sQuery(id+"F14.wireOp",EDGE,"E137"),sQuery(id+"F14.wireOp",EDGE,"E138"),sQuery(id+"F14.wireOp",EDGE,"E139"),sQuery(id+"F14.wireOp",EDGE,"E140"),sQuery(id+"F14.wireOp",EDGE,"E141"),sQuery(id+"F14.wireOp",EDGE,"E142"),sQuery(id+"F14.wireOp",EDGE,"E143"),sQuery(id+"F14.wireOp",EDGE,"E144"),sQuery(id+"F14.wireOp",EDGE,"E145")])],"isStart":false})});
            var Q3;
            Q3=makeQuery(id+"F15.boolean.opBoolean","COPY",FACE,{"derivedFrom":makeQuery(id+"F15.opExtrude","CAP_FACE",FACE,{"disambiguationData":[OSD([sQuery(id+"F14.wireOp",EDGE,"E146"),sQuery(id+"F14.wireOp",EDGE,"E147"),sQuery(id+"F14.wireOp",EDGE,"E148"),sQuery(id+"F14.wireOp",EDGE,"E149"),sQuery(id+"F14.wireOp",EDGE,"E150"),sQuery(id+"F14.wireOp",EDGE,"E151"),sQuery(id+"F14.wireOp",EDGE,"E152"),sQuery(id+"F14.wireOp",EDGE,"E153"),sQuery(id+"F14.wireOp",EDGE,"E154"),sQuery(id+"F14.wireOp",EDGE,"E155"),sQuery(id+"F14.wireOp",EDGE,"E156"),sQuery(id+"F14.wireOp",EDGE,"E157"),sQuery(id+"F14.wireOp",EDGE,"E158"),sQuery(id+"F14.wireOp",EDGE,"E159")])],"isStart":false})});
            extrude(context, id + "F24", {"entities" : qUnion([Q0, Q1, Q2, Q3]), "depth" : 0.8 * mm, "offsetDistance" : 25.4 * mm});
        }
        {
            var Q0;
            Q0=makeQuery(id+"F17.boolean.opBoolean","COPY",FACE,{"derivedFrom":makeQuery(id+"F17.opExtrude","CAP_FACE",FACE,{"disambiguationData":[OSD([sQuery(id+"F16.wireOp",EDGE,"E162"),sQuery(id+"F16.wireOp",EDGE,"E163"),sQuery(id+"F16.wireOp",EDGE,"E164"),sQuery(id+"F16.wireOp",EDGE,"E165"),sQuery(id+"F16.wireOp",EDGE,"E166"),sQuery(id+"F16.wireOp",EDGE,"E167"),sQuery(id+"F16.wireOp",EDGE,"E168"),sQuery(id+"F16.wireOp",EDGE,"E169"),sQuery(id+"F16.wireOp",EDGE,"E170"),sQuery(id+"F16.wireOp",EDGE,"E171"),sQuery(id+"F16.wireOp",EDGE,"E172"),sQuery(id+"F16.wireOp",EDGE,"E173"),sQuery(id+"F16.wireOp",EDGE,"E174"),sQuery(id+"F16.wireOp",EDGE,"E175")])],"isStart":false})});
            var Q1;
            Q1=makeQuery(id+"F17.boolean.opBoolean","COPY",FACE,{"derivedFrom":makeQuery(id+"F17.opExtrude","CAP_FACE",FACE,{"disambiguationData":[OSD([sQuery(id+"F16.wireOp",EDGE,"E176"),sQuery(id+"F16.wireOp",EDGE,"E177"),sQuery(id+"F16.wireOp",EDGE,"E178"),sQuery(id+"F16.wireOp",EDGE,"E179")])],"isStart":false})});
            var Q2;
            Q2=makeQuery(id+"F19.boolean.opBoolean","COPY",FACE,{"derivedFrom":makeQuery(id+"F19.opExtrude","CAP_FACE",FACE,{"disambiguationData":[OSD([sQuery(id+"F18.wireOp",EDGE,"E180"),sQuery(id+"F18.wireOp",EDGE,"E181"),sQuery(id+"F18.wireOp",EDGE,"E182"),sQuery(id+"F18.wireOp",EDGE,"E183"),sQuery(id+"F18.wireOp",EDGE,"E184"),sQuery(id+"F18.wireOp",EDGE,"E185"),sQuery(id+"F18.wireOp",EDGE,"E186"),sQuery(id+"F18.wireOp",EDGE,"E187"),sQuery(id+"F18.wireOp",EDGE,"E188"),sQuery(id+"F18.wireOp",EDGE,"E189"),sQuery(id+"F18.wireOp",EDGE,"E190"),sQuery(id+"F18.wireOp",EDGE,"E191"),sQuery(id+"F18.wireOp",EDGE,"E192"),sQuery(id+"F18.wireOp",EDGE,"E193")])],"isStart":false})});
            var Q3;
            Q3=makeQuery(id+"F19.boolean.opBoolean","COPY",FACE,{"derivedFrom":makeQuery(id+"F19.opExtrude","CAP_FACE",FACE,{"disambiguationData":[OSD([sQuery(id+"F18.wireOp",EDGE,"E194"),sQuery(id+"F18.wireOp",EDGE,"E195"),sQuery(id+"F18.wireOp",EDGE,"E196"),sQuery(id+"F18.wireOp",EDGE,"E197"),sQuery(id+"F18.wireOp",EDGE,"E198"),sQuery(id+"F18.wireOp",EDGE,"E199"),sQuery(id+"F18.wireOp",EDGE,"E200"),sQuery(id+"F18.wireOp",EDGE,"E201"),sQuery(id+"F18.wireOp",EDGE,"E202"),sQuery(id+"F18.wireOp",EDGE,"E203"),sQuery(id+"F18.wireOp",EDGE,"E204"),sQuery(id+"F18.wireOp",EDGE,"E205"),sQuery(id+"F18.wireOp",EDGE,"E206"),sQuery(id+"F18.wireOp",EDGE,"E207")])],"isStart":false})});
            extrude(context, id + "F25", {"entities" : qUnion([Q0, Q1, Q2, Q3]), "depth" : 0.8 * mm, "offsetDistance" : 25.4 * mm});
        }
        {
            var Q0;
            Q0=makeQuery(id+"F9.boolean.opBoolean","COPY",FACE,{"derivedFrom":makeQuery(id+"F9.opExtrude","CAP_FACE",FACE,{"disambiguationData":[OSD([sQuery(id+"F8.wireOp",EDGE,"E20"),sQuery(id+"F8.wireOp",EDGE,"E21"),sQuery(id+"F8.wireOp",EDGE,"E22"),sQuery(id+"F8.wireOp",EDGE,"E23"),sQuery(id+"F8.wireOp",EDGE,"E24"),sQuery(id+"F8.wireOp",EDGE,"E25"),sQuery(id+"F8.wireOp",EDGE,"E26"),sQuery(id+"F8.wireOp",EDGE,"E27"),sQuery(id+"F8.wireOp",EDGE,"E28"),sQuery(id+"F8.wireOp",EDGE,"E29"),sQuery(id+"F8.wireOp",EDGE,"E30"),sQuery(id+"F8.wireOp",EDGE,"E31"),sQuery(id+"F8.wireOp",EDGE,"E32"),sQuery(id+"F8.wireOp",EDGE,"E33")])],"isStart":false})});
            var Q1;
            Q1=makeQuery(id+"F9.boolean.opBoolean","COPY",FACE,{"derivedFrom":makeQuery(id+"F9.opExtrude","CAP_FACE",FACE,{"disambiguationData":[OSD([sQuery(id+"F8.wireOp",EDGE,"E34"),sQuery(id+"F8.wireOp",EDGE,"E35"),sQuery(id+"F8.wireOp",EDGE,"E36"),sQuery(id+"F8.wireOp",EDGE,"E37")])],"isStart":false})});
            var Q2;
            Q2=makeQuery(id+"F9.boolean.opBoolean","COPY",FACE,{"derivedFrom":makeQuery(id+"F9.opExtrude","CAP_FACE",FACE,{"disambiguationData":[OSD([sQuery(id+"F8.wireOp",EDGE,"E38"),sQuery(id+"F8.wireOp",EDGE,"E39"),sQuery(id+"F8.wireOp",EDGE,"E40"),sQuery(id+"F8.wireOp",EDGE,"E41"),sQuery(id+"F8.wireOp",EDGE,"E42"),sQuery(id+"F8.wireOp",EDGE,"E43"),sQuery(id+"F8.wireOp",EDGE,"E44"),sQuery(id+"F8.wireOp",EDGE,"E45"),sQuery(id+"F8.wireOp",EDGE,"E46"),sQuery(id+"F8.wireOp",EDGE,"E47"),sQuery(id+"F8.wireOp",EDGE,"E48"),sQuery(id+"F8.wireOp",EDGE,"E49"),sQuery(id+"F8.wireOp",EDGE,"E50"),sQuery(id+"F8.wireOp",EDGE,"E51")])],"isStart":false})});
            var Q3;
            Q3=makeQuery(id+"F9.boolean.opBoolean","COPY",FACE,{"derivedFrom":makeQuery(id+"F9.opExtrude","CAP_FACE",FACE,{"disambiguationData":[OSD([sQuery(id+"F8.wireOp",EDGE,"E52"),sQuery(id+"F8.wireOp",EDGE,"E53"),sQuery(id+"F8.wireOp",EDGE,"E54"),sQuery(id+"F8.wireOp",EDGE,"E55"),sQuery(id+"F8.wireOp",EDGE,"E56"),sQuery(id+"F8.wireOp",EDGE,"E57"),sQuery(id+"F8.wireOp",EDGE,"E58"),sQuery(id+"F8.wireOp",EDGE,"E59"),sQuery(id+"F8.wireOp",EDGE,"E60"),sQuery(id+"F8.wireOp",EDGE,"E61"),sQuery(id+"F8.wireOp",EDGE,"E62"),sQuery(id+"F8.wireOp",EDGE,"E63"),sQuery(id+"F8.wireOp",EDGE,"E64"),sQuery(id+"F8.wireOp",EDGE,"E65")])],"isStart":false})});
            extrude(context, id + "F26", {"entities" : qUnion([Q0, Q1, Q2, Q3]), "depth" : 0.8 * mm, "offsetDistance" : 25.4 * mm});
        }
        {
            var Q0;
            Q0=makeQuery(id+"F23.opExtrude","SWEPT_FACE",FACE,{"disambiguationData":[OSD([sQuery(id+"F10.wireOp",EDGE,"E90")])]});
            var sketch = newSketch(context, id + "F27", { "sketchPlane" : qUnion([Q0])});
            skArc(sketch, "E208", {"start": v(41.91, 44.83) * mm, "mid": v(41.28, 44.95) * mm, "end": v(40.64, 44.99) * mm});
            skSolve(sketch);
        }
        {
            var Q0;
            {var subQ0=sQuery(id+"F27.wireOp",EDGE,"E208");Q0=makeQuery(id+"F27.imprint","IMPRINT",FACE,{"disambiguationData":[TD([[makeQuery(id+"F27.imprint","IMPRINT",EDGE,{"derivedFrom":subQ0}),-1.0]])]});}
            extrude(context, id + "F28", {"entities" : qUnion([Q0]), "operationType" : NewBodyOperationType.REMOVE, "oppositeDirection" : true, "depth" : 25.4 * mm, "offsetDistance" : 25.4 * mm});
        }
        {
            var Q0;
            Q0=makeQuery(id+"F23.opExtrude","SWEPT_FACE",FACE,{"disambiguationData":[OSD([sQuery(id+"F10.wireOp",EDGE,"E69")])]});
            var sketch = newSketch(context, id + "F29", { "sketchPlane" : qUnion([Q0])});
            skArc(sketch, "E209", {"start": v(23.5, 44.99) * mm, "mid": v(23.18, 44.97) * mm, "end": v(22.86, 44.92) * mm});
            skSolve(sketch);
        }
        {
            var Q0;
            {var subQ0=sQuery(id+"F29.wireOp",EDGE,"E209");Q0=makeQuery(id+"F29.imprint","IMPRINT",FACE,{"disambiguationData":[TD([[makeQuery(id+"F29.imprint","IMPRINT",EDGE,{"derivedFrom":subQ0}),-1.0]])]});}
            extrude(context, id + "F30", {"entities" : qUnion([Q0]), "operationType" : NewBodyOperationType.REMOVE, "oppositeDirection" : true, "depth" : 25.4 * mm, "offsetDistance" : 25.4 * mm});
        }
        {
            var Q0;
            Q0=makeQuery(id+"F25.opExtrude","SWEPT_FACE",FACE,{"disambiguationData":[OSD([sQuery(id+"F18.wireOp",EDGE,"E181")])]});
            var sketch = newSketch(context, id + "F31", { "sketchPlane" : qUnion([Q0])});
            skArc(sketch, "E210", {"start": v(-3.18, -38.83) * mm, "mid": v(-2.86, -38.82) * mm, "end": v(-2.54, -38.77) * mm});
            skSolve(sketch);
        }
        {
            var Q0;
            {var subQ0=sQuery(id+"F31.wireOp",EDGE,"E210");Q0=makeQuery(id+"F31.imprint","IMPRINT",FACE,{"disambiguationData":[TD([[makeQuery(id+"F31.imprint","IMPRINT",EDGE,{"derivedFrom":subQ0}),-1.0]])]});}
            extrude(context, id + "F32", {"entities" : qUnion([Q0]), "operationType" : NewBodyOperationType.REMOVE, "oppositeDirection" : true, "depth" : 25.4 * mm, "offsetDistance" : 25.4 * mm});
        }
    });
